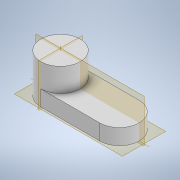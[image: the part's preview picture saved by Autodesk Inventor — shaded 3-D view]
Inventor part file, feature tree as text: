
AUTODESK INVENTOR PART (.ipt)
format: ipt  version: 2022.4 (Build 264492010, 492A)  size: 114,688 bytes
history: native  units: mm
features: extrude x2, sketch x1
ambient origin geometry x8: Origin, YZ Plane, XZ Plane, XY Plane, X Axis, Y Axis, Z Axis, Center Point
bodies: Solid1 (feature_tree)
feature tree (3):
  sketch  "Sketch1"  dims[d0=5.0mm d1=7.5mm d3=5.0mm d4=0.0mm d5=2.0mm d6=0.0mm d13=7.5mm]
  extrude  "Extrusion1"  Depth=7.5mm
  extrude  "Extrusion2"  Depth=5.0mm TaperAngle=0.0deg
